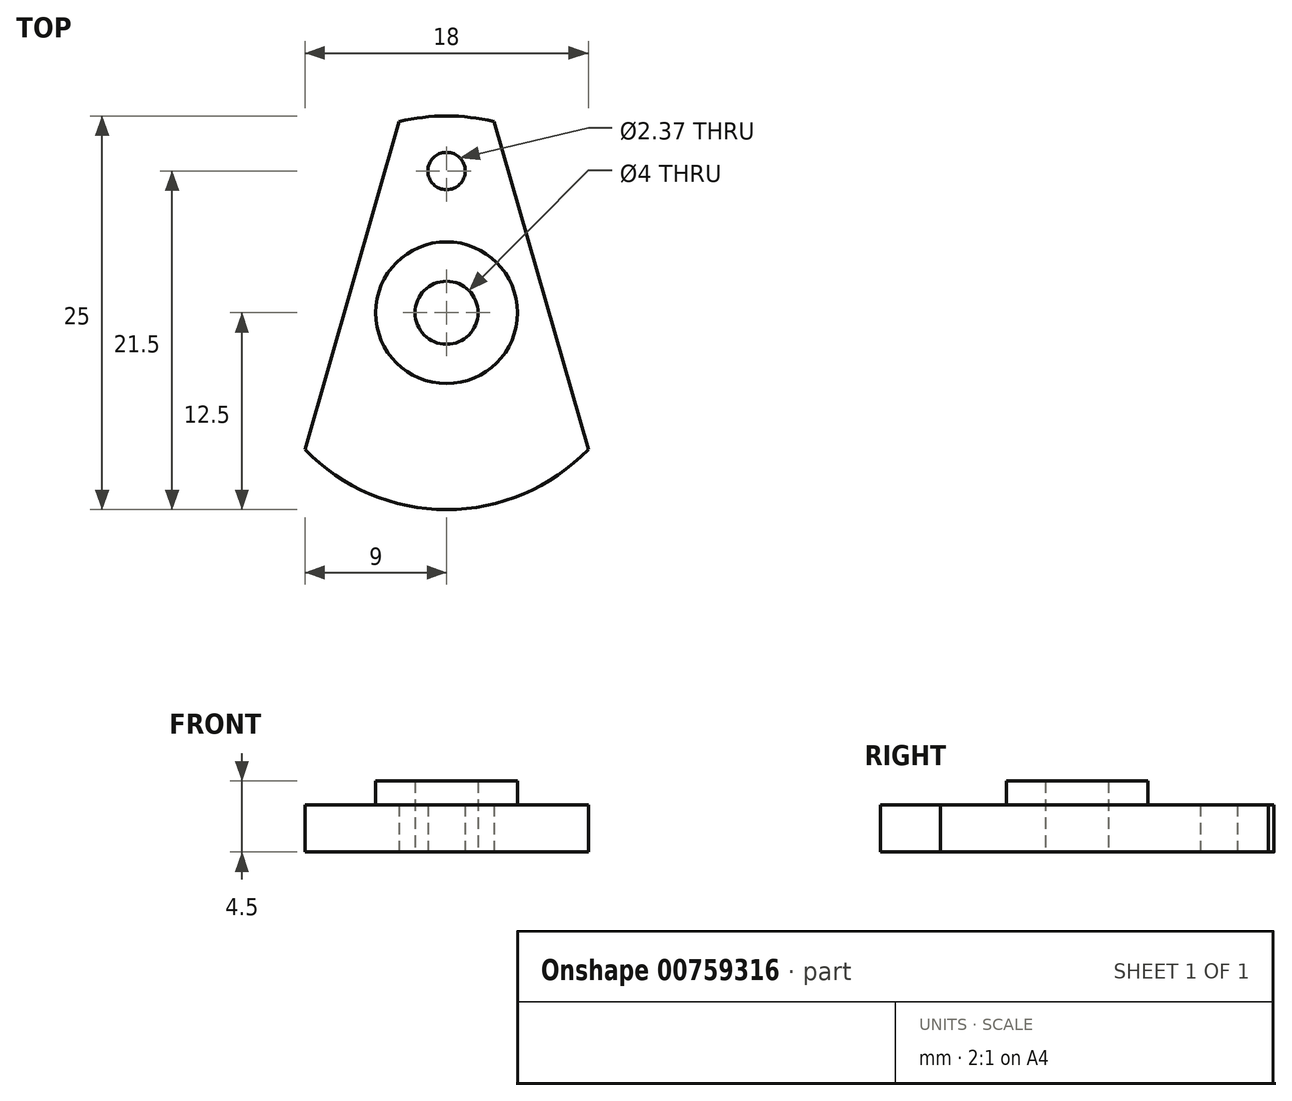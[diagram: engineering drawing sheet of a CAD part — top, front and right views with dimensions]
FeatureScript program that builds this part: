
annotation { "Feature Type Name" : "Feature", "Feature Type Description" : "" }
export const myFeature = defineFeature(function(context is Context, id is Id, definition is map)
    precondition{}
    {
        {
            var Q0;
            Q0=qCreatedBy(makeId("Top.planeOp"),FACE);
            var sketch = newSketch(context, id + "F0", { "sketchPlane" : qUnion([Q0])});
            skArc(sketch, "E0", {"start": v(-9, -8.67) * mm, "mid": v(0, -12.5) * mm, "end": v(9, -8.67) * mm});
            skPoint(sketch, "E1.end.orphan", {"position": v(0, 15.5) * mm});
            skPoint(sketch, "E2.start.orphan", {"position": v(-16.21, 0) * mm});
            skLineSegment(sketch, "E3", {"start": v(3, 12.13) * mm, "end": v(9, -8.67) * mm});
            skLineSegment(sketch, "E4.MirrorCS", {"start": v(-3, 12.13) * mm, "end": v(-9, -8.67) * mm});
            skArc(sketch, "E5.trimOffspring", {"start": v(3, 12.13) * mm, "mid": v(0, 12.5) * mm, "end": v(-3, 12.13) * mm});
            skCircle(sketch, "E6", {"center": v(0, 9) * mm, "radius": 1.19 * mm});
            skCircle(sketch, "E7", {"center": v(0, 0) * mm, "radius": 4.5 * mm});
            skCircle(sketch, "E8", {"center": v(0, 0) * mm, "radius": 2 * mm});
            skSolve(sketch);
        }
        {
            var Q0;
            Q0=makeQuery(id+"F0.imprint","IMPRINT",FACE,{"disambiguationData":[TD([[makeQuery(id+"F0.imprint","IMPRINT",EDGE,{"derivedFrom":sQuery(id+"F0.wireOp",EDGE,"E0")}),1.0]])]});
            extrude(context, id + "F1", {"entities" : qUnion([Q0]), "depth" : 3 * mm, "offsetDistance" : 25 * mm});
        }
        {
            var Q0;
            Q0=makeQuery(id+"F0.imprint","IMPRINT",FACE,{"disambiguationData":[TD([[makeQuery(id+"F0.imprint","IMPRINT",EDGE,{"derivedFrom":sQuery(id+"F0.wireOp",EDGE,"E7")}),1.0]])]});
            extrude(context, id + "F2", {"entities" : qUnion([Q0]), "operationType" : NewBodyOperationType.ADD, "depth" : 4.5 * mm, "offsetDistance" : 25 * mm});
        }
    });
